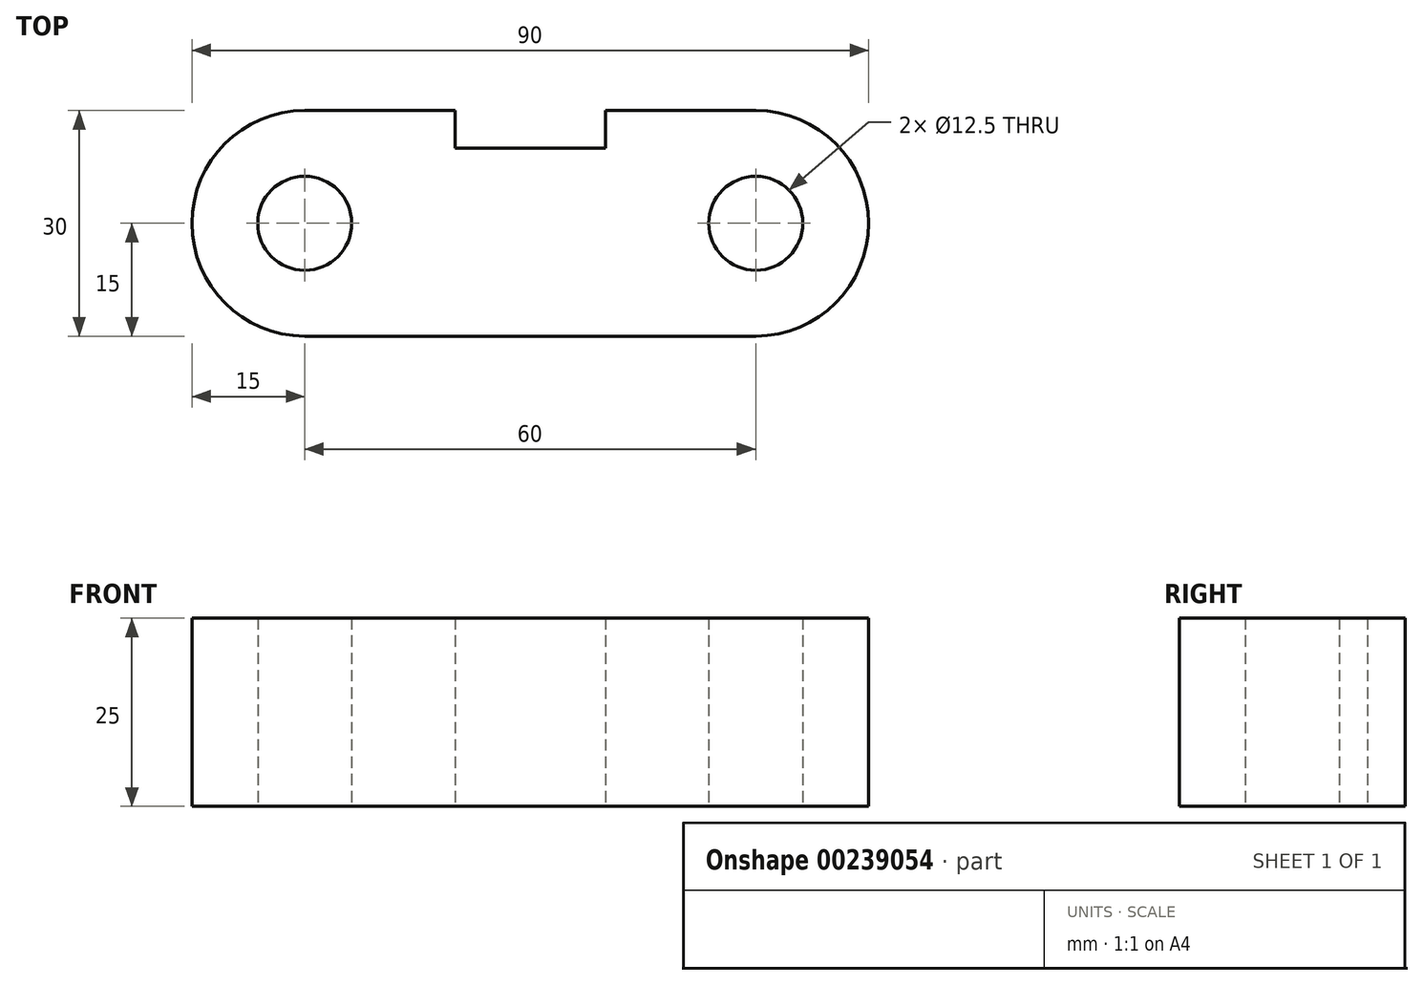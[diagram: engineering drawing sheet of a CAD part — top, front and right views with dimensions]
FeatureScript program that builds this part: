
annotation { "Feature Type Name" : "Feature", "Feature Type Description" : "" }
export const myFeature = defineFeature(function(context is Context, id is Id, definition is map)
    precondition{}
    {
        {
            var Q0;
            Q0=qCreatedBy(makeId("Top.planeOp"),FACE);
            var sketch = newSketch(context, id + "F0", { "sketchPlane" : qUnion([Q0])});
            skCircle(sketch, "E0", {"center": v(0, 0) * mm, "radius": 6.25 * mm});
            skLineSegment(sketch, "E1", {"start": v(0, 0) * mm, "end": v(60, 0) * mm, "construction": true});
            skCircle(sketch, "E2", {"center": v(60, 0) * mm, "radius": 6.25 * mm});
            skArc(sketch, "E3", {"start": v(0, 15) * mm, "mid": v(-15, 0) * mm, "end": v(0, -15) * mm});
            skArc(sketch, "E4", {"start": v(60, -15) * mm, "mid": v(75, 0) * mm, "end": v(60, 15) * mm});
            skLineSegment(sketch, "E5", {"start": v(0, 15) * mm, "end": v(20, 15) * mm});
            skLineSegment(sketch, "E6", {"start": v(20, 15) * mm, "end": v(20, 10) * mm});
            skLineSegment(sketch, "E7", {"start": v(20, 10) * mm, "end": v(40, 10) * mm});
            skLineSegment(sketch, "E8", {"start": v(40, 10) * mm, "end": v(40, 15) * mm});
            skLineSegment(sketch, "E9", {"start": v(40, 15) * mm, "end": v(60, 15) * mm});
            skLineSegment(sketch, "E10", {"start": v(0, -15) * mm, "end": v(60, -15) * mm});
            skSolve(sketch);
        }
        {
            var Q0;
            Q0=makeQuery(id+"F0.imprint","IMPRINT",FACE,{"disambiguationData":[TD([[makeQuery(id+"F0.imprint","IMPRINT",EDGE,{"derivedFrom":sQuery(id+"F0.wireOp",EDGE,"E0")}),-1.0]])]});
            extrude(context, id + "F1", {"entities" : qUnion([Q0]), "depth" : 25 * mm});
        }
    });
